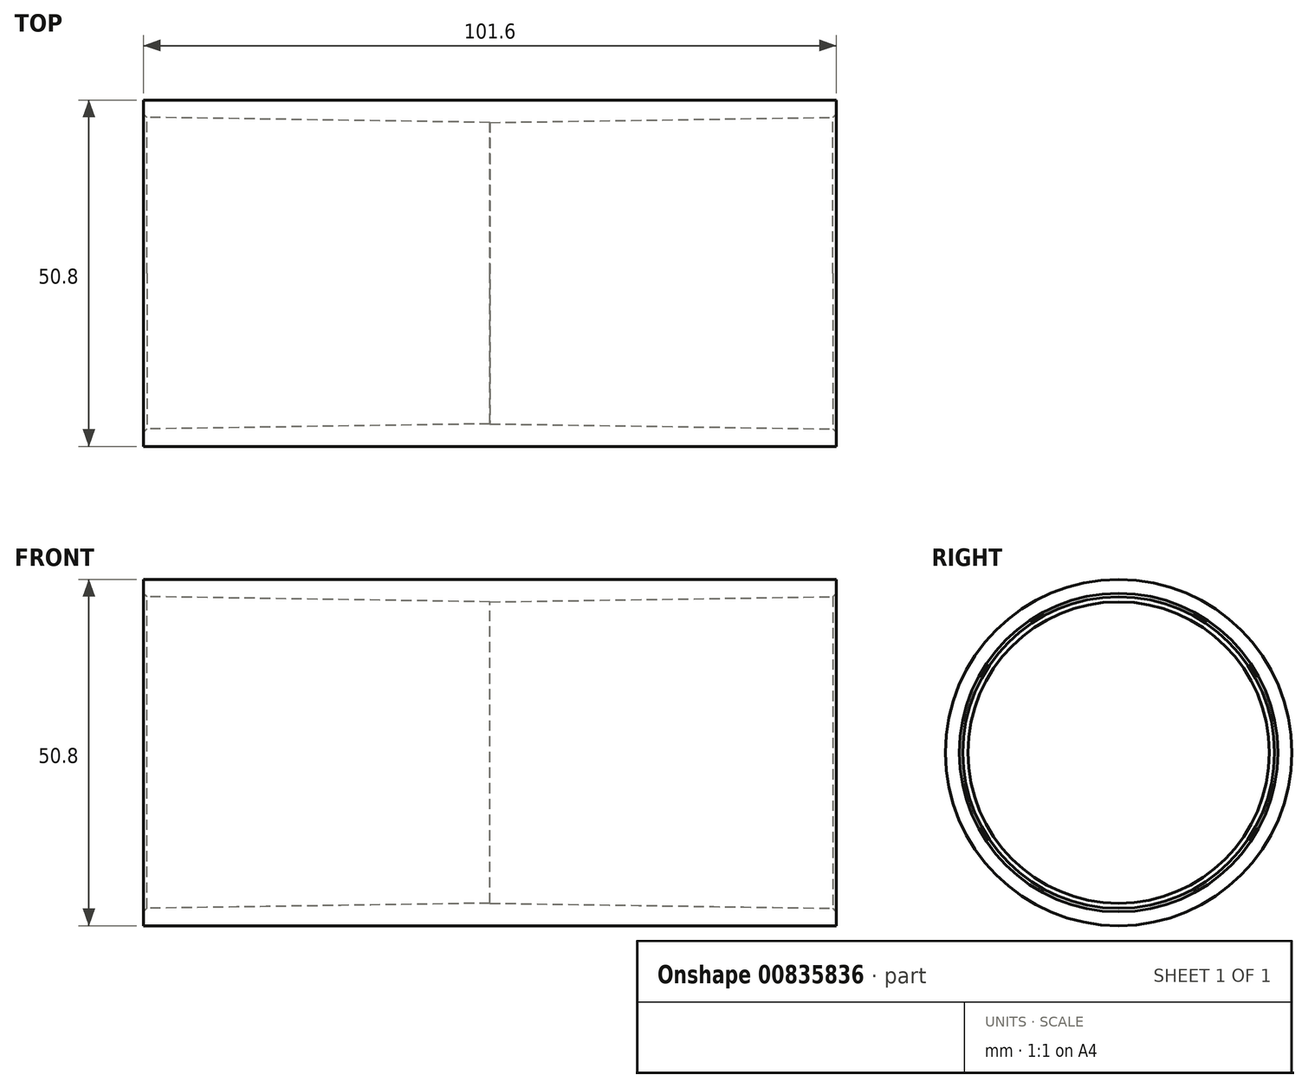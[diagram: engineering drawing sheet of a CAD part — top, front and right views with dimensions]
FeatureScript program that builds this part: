
annotation { "Feature Type Name" : "Feature", "Feature Type Description" : "" }
export const myFeature = defineFeature(function(context is Context, id is Id, definition is map)
    precondition{}
    {
        {
            var Q0;
            Q0=qCreatedBy(makeId("Front.planeOp"),FACE);
            var sketch = newSketch(context, id + "F0", { "sketchPlane" : qUnion([Q0])});
            skLineSegment(sketch, "E0", {"start": v(0, 0) * mm, "end": v(-103.9, 0) * mm, "construction": true});
            skLineSegment(sketch, "E1", {"start": v(0, 25.4) * mm, "end": v(0, 22.1) * mm});
            skLineSegment(sketch, "E2", {"start": v(0, 22.1) * mm, "end": v(50.8, 22.86) * mm});
            skLineSegment(sketch, "E3", {"start": v(50.8, 22.86) * mm, "end": v(50.8, 25.4) * mm});
            skLineSegment(sketch, "E4", {"start": v(50.8, 25.4) * mm, "end": v(0, 25.4) * mm});
            skPoint(sketch, "E5", {"position": v(25.4, 22.48) * mm});
            skSolve(sketch);
        }
        {
            var Q0;
            Q0 = qSketchRegion(id + "F0", true);
            var Q1;
            Q1=sQuery(id+"F0.wireOp",EDGE,"E0");
            revolve(context, id + "F1", {"surfaceOperationType" : NewSurfaceOperationType.NEW, "entities" : qUnion([Q0]), "axis" : qUnion([Q1]), "revolveType" : RevolveType.FULL});
        }
        {
            var Q0;
            Q0=makeQuery(id+"F1.opRevolve","SWEPT_BODY",BODY,{"disambiguationData":[OSD([sQuery(id+"F0.wireOp",EDGE,"E1"),sQuery(id+"F0.wireOp",EDGE,"E2"),sQuery(id+"F0.wireOp",EDGE,"E3"),sQuery(id+"F0.wireOp",EDGE,"E4")])]});
            var Q1;
            Q1=makeQuery(id+"F1.opRevolve","SWEPT_FACE",FACE,{"disambiguationData":[OSD([sQuery(id+"F0.wireOp",EDGE,"E1")])]});
            mirror(context, id + "F2", {"operationType" : NewBodyOperationType.ADD, "entities" : qUnion([Q0]), "mirrorPlane" : qUnion([Q1])});
        }
        {
            var Q0;
            Q0=makeQuery(id+"F2.opPattern","COPY",EDGE,{"derivedFrom":makeQuery(id+"F1.opRevolve","SWEPT_EDGE",EDGE,{"disambiguationData":[OSD([sQuery(id+"F0.wireOp",EDGE,"E2"),sQuery(id+"F0.wireOp",EDGE,"E3")])]}),"instanceName":"1"});
            var Q1;
            Q1=makeQuery(id+"F1.opRevolve","SWEPT_EDGE",EDGE,{"disambiguationData":[OSD([sQuery(id+"F0.wireOp",EDGE,"E2"),sQuery(id+"F0.wireOp",EDGE,"E3")])]});
            chamfer(context, id + "F3", {"entities" : qUnion([Q0, Q1]), "width" : 0.5 * mm, "tangentPropagation" : true});
        }
    });
